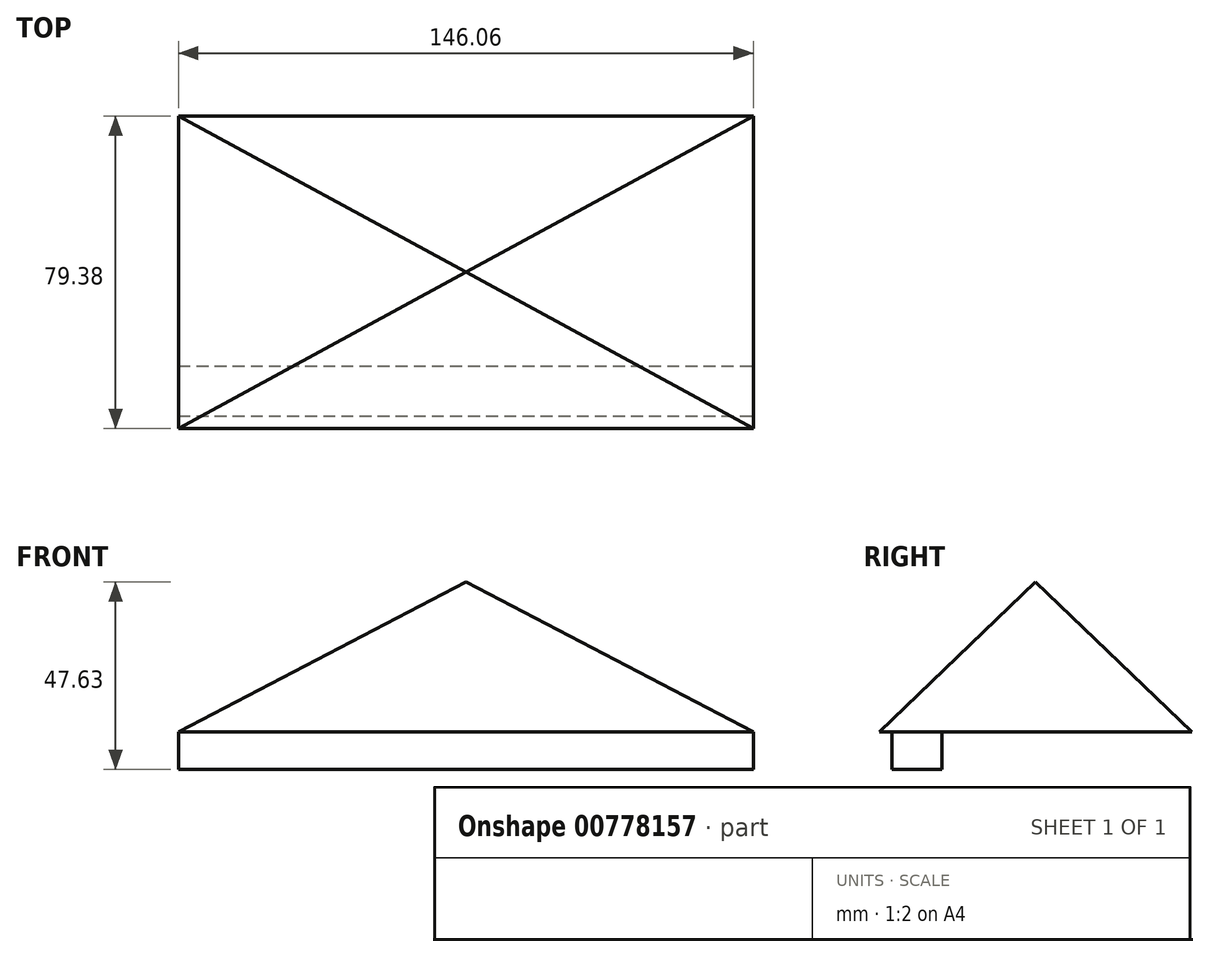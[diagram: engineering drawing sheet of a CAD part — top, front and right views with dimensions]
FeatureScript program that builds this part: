
annotation { "Feature Type Name" : "Feature", "Feature Type Description" : "" }
export const myFeature = defineFeature(function(context is Context, id is Id, definition is map)
    precondition{}
    {
        {
            var Q0;
            Q0=qCreatedBy(makeId("Top.planeOp"),FACE);
            var sketch = newSketch(context, id + "F0", { "sketchPlane" : qUnion([Q0])});
            skLineSegment(sketch, "E0", {"start": v(-73.03, 39.69) * mm, "end": v(-73.03, -39.69) * mm});
            skLineSegment(sketch, "E1", {"start": v(-73.03, -39.69) * mm, "end": v(73.03, -39.69) * mm});
            skLineSegment(sketch, "E2", {"start": v(73.03, -39.69) * mm, "end": v(73.03, 39.69) * mm});
            skLineSegment(sketch, "E3", {"start": v(73.03, 39.69) * mm, "end": v(-73.03, 39.69) * mm});
            skPoint(sketch, "E4", {"position": v(-73.02, 0) * mm});
            skPoint(sketch, "E5", {"position": v(73.03, 0) * mm});
            skLineSegment(sketch, "E6", {"start": v(-73.02, 0) * mm, "end": v(0, 0) * mm, "construction": true});
            skLineSegment(sketch, "E7", {"start": v(0, 0) * mm, "end": v(73.03, 0) * mm, "construction": true});
            skLineSegment(sketch, "E8", {"start": v(0, 39.69) * mm, "end": v(0, 0) * mm, "construction": true});
            skLineSegment(sketch, "E9", {"start": v(0, 0) * mm, "end": v(0, -39.69) * mm, "construction": true});
            skSolve(sketch);
        }
        {
            var Q0;
            Q0=qCreatedBy(makeId("Top.planeOp"),FACE);
            cPlane(context, id + "F1", {"entities" : qUnion([Q0]), "cplaneType" : CPlaneType.OFFSET, "offset" : 38.1 * mm, "width" : 152.4 * mm, "height" : 152.4 * mm});
        }
        {
            var Q0;
            Q0=qCreatedBy(id+"F1.planeOp",FACE);
            var sketch = newSketch(context, id + "F2", { "sketchPlane" : qUnion([Q0])});
            skPoint(sketch, "E10", {"position": v(0, 0) * mm});
            skSolve(sketch);
        }
        {
            var Q0;
            Q0=makeQuery(id+"F0.imprint","IMPRINT",FACE,{"disambiguationData":[TD([[makeQuery(id+"F0.imprint","IMPRINT",EDGE,{"derivedFrom":sQuery(id+"F0.wireOp",EDGE,"E0")}),1.0]])]});
            var Q1;
            Q1=sQuery(id+"F2.wireOp",VERTEX,"E10");
            loft(context, id + "F3", {"sheetProfilesArray" : [{ "sheetProfileEntities" : qUnion([Q0]) }, { "sheetProfileEntities" : qUnion([Q1]) }]});
        }
        {
            var Q0;
            Q0=qCreatedBy(makeId("Top.planeOp"),FACE);
            cPlane(context, id + "F4", {"entities" : qUnion([Q0]), "cplaneType" : CPlaneType.OFFSET, "offset" : 0 * mm, "oppositeDirection" : true, "width" : 152.4 * mm, "height" : 152.4 * mm});
        }
        {
            var Q0;
            Q0=qCreatedBy(id+"F4.planeOp",FACE);
            var sketch = newSketch(context, id + "F5", { "sketchPlane" : qUnion([Q0])});
            skLineSegment(sketch, "E11.bottom", {"start": v(-73.03, -36.51) * mm, "end": v(73.03, -36.51) * mm});
            skLineSegment(sketch, "E11.top", {"start": v(-73.03, -23.81) * mm, "end": v(73.03, -23.81) * mm});
            skLineSegment(sketch, "E11.left", {"start": v(-73.03, -36.51) * mm, "end": v(-73.03, -23.81) * mm});
            skLineSegment(sketch, "E11.right", {"start": v(73.03, -36.51) * mm, "end": v(73.03, -23.81) * mm});
            skLineSegment(sketch, "E12", {"start": v(0, -36.51) * mm, "end": v(0, 0) * mm, "construction": true});
            skPoint(sketch, "E12.startSnap0", {"position": v(0, -36.51) * mm});
            skLineSegment(sketch, "E13", {"start": v(0, 0) * mm, "end": v(-73.03, 0) * mm, "construction": true});
            skLineSegment(sketch, "E14", {"start": v(0, 0) * mm, "end": v(73.03, 0) * mm, "construction": true});
            skLineSegment(sketch, "E15", {"start": v(0, -23.81) * mm, "end": v(0, 0) * mm, "construction": true});
            skLineSegment(sketch, "E16", {"start": v(-73.03, 0) * mm, "end": v(-73.03, -39.7) * mm, "construction": true});
            skLineSegment(sketch, "E17", {"start": v(-73.03, -30.16) * mm, "end": v(-73.03, -30.16) * mm});
            skLineSegment(sketch, "E18", {"start": v(73.03, 0) * mm, "end": v(73.03, -40.43) * mm, "construction": true});
            skLineSegment(sketch, "E19", {"start": v(73.03, -30.16) * mm, "end": v(73.03, -30.16) * mm});
            skSolve(sketch);
        }
        {
            var Q0;
            Q0=makeQuery(id+"F5.imprint","IMPRINT",FACE,{"disambiguationData":[TD([[makeQuery(id+"F5.imprint","IMPRINT",EDGE,{"derivedFrom":sQuery(id+"F5.wireOp",EDGE,"E11.bottom")}),1.0]])]});
            extrude(context, id + "F6", {"entities" : qUnion([Q0]), "operationType" : NewBodyOperationType.ADD, "oppositeDirection" : true, "depth" : 9.52 * mm, "offsetDistance" : 25.4 * mm});
        }
    });
